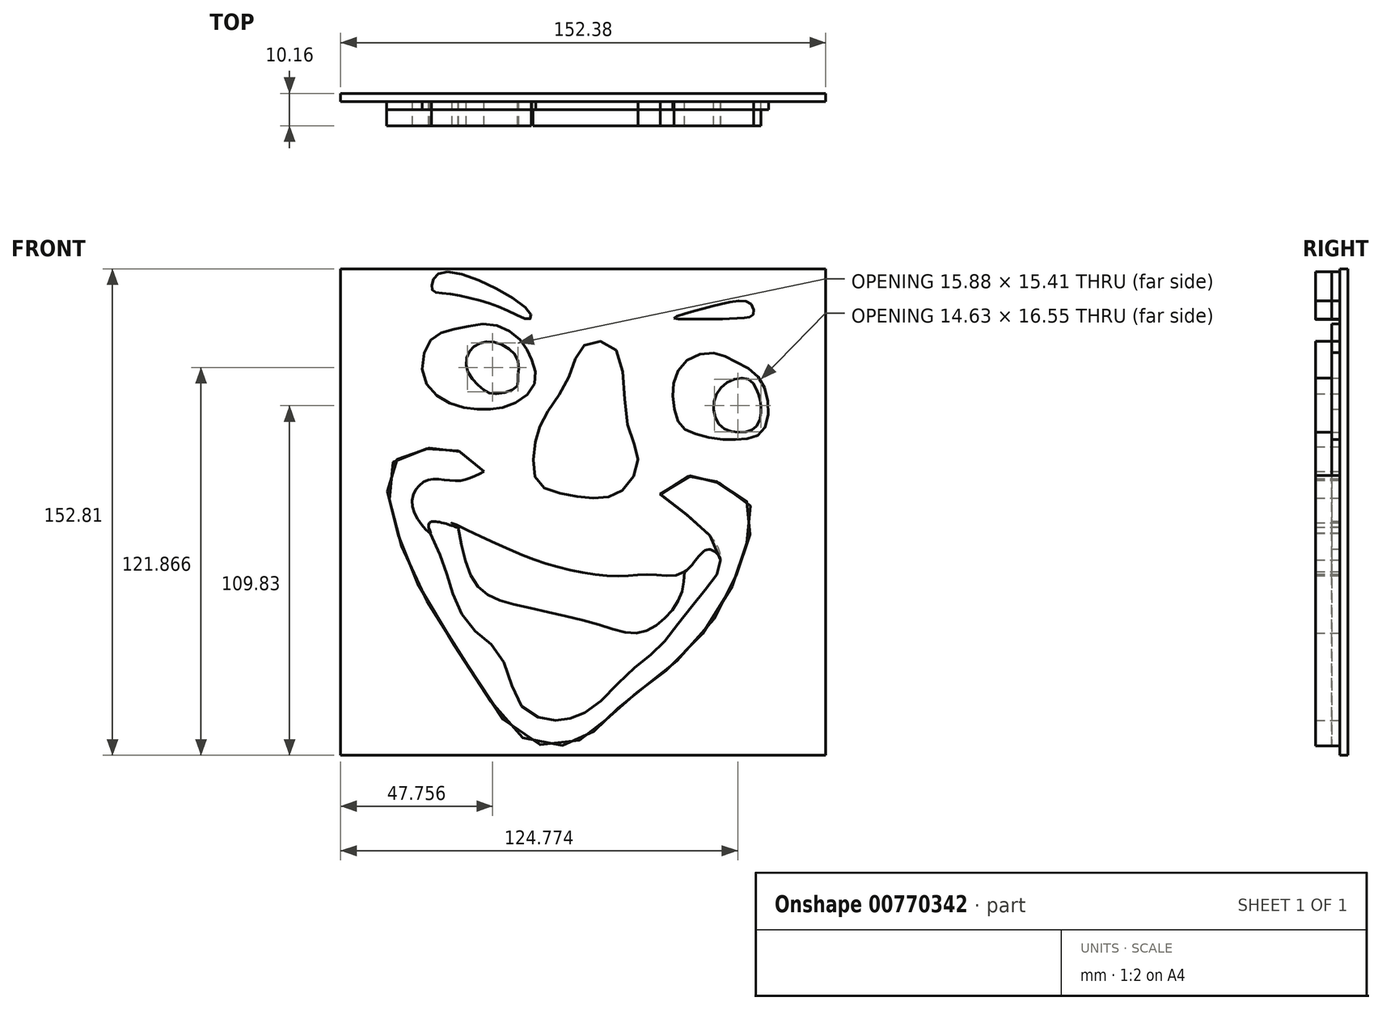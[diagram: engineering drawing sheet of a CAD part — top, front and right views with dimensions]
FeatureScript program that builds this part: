
annotation { "Feature Type Name" : "Feature", "Feature Type Description" : "" }
export const myFeature = defineFeature(function(context is Context, id is Id, definition is map)
    precondition{}
    {
        {
            var Q0;
            Q0=qCreatedBy(makeId("Front.planeOp"),FACE);
            var sketch = newSketch(context, id + "F0", { "sketchPlane" : qUnion([Q0])});
            skFitSpline(sketch, "E0", {"points": [v(-16.48, 48.25) * mm, v(-15.6, 40.6) * mm, v(-23.03, 34.06) * mm, v(-31.76, 32.75) * mm, v(-41.8, 34.5) * mm, v(-50.32, 42.57) * mm, v(-48.14, 54.58) * mm, v(-39.84, 58.07) * mm, v(-28.7, 59.38) * mm, v(-20.2, 54.58) * mm, v(-16.48, 48.25) * mm]});
            skFitSpline(sketch, "E1", {"points": [v(-25.87, 53.05) * mm, v(-32.2, 53.7) * mm, v(-36.13, 50.65) * mm, v(-36.78, 45.19) * mm, v(-32.42, 39.51) * mm, v(-27.83, 37.55) * mm, v(-21.29, 39.73) * mm, v(-20.85, 42.57) * mm, v(-20.85, 48.25) * mm, v(-25.87, 53.05) * mm]});
            skFitSpline(sketch, "E2", {"points": [v(40.71, 50.43) * mm, v(32.42, 48.25) * mm, v(28.27, 41.7) * mm, v(28.05, 34.27) * mm, v(30.24, 27.72) * mm, v(34.6, 25.1) * mm, v(42.9, 23.36) * mm, v(49.67, 23.36) * mm, v(54.9, 24.67) * mm, v(57.74, 29.9) * mm, v(57.09, 38.2) * mm, v(53.38, 44.32) * mm, v(46.4, 48.25) * mm, v(40.71, 50.43) * mm]});
            skFitSpline(sketch, "E3", {"points": [v(0, 52.83) * mm, v(-4.91, 42.57) * mm, v(-12.55, 30.13) * mm, v(-15.6, 20.74) * mm, v(-14.74, 10.04) * mm, v(-6.66, 6.11) * mm, v(3.6, 4.8) * mm, v(11.68, 6.99) * mm, v(16.92, 16.8) * mm, v(13.43, 28.82) * mm, v(9.71, 51.74) * mm, v(0, 52.83) * mm]});
            skFitSpline(sketch, "E4", {"points": [v(-42.9, 75.92) * mm, v(-17.14, 63.3) * mm, v(-17.14, 61.13) * mm, v(-24.12, 63.75) * mm, v(-33.95, 67.24) * mm, v(-43.99, 69.2) * mm, v(-47.48, 69.86) * mm, v(-47.7, 72.7) * mm, v(-42.9, 75.92) * mm]});
            skFitSpline(sketch, "E5", {"points": [v(28.27, 61.34) * mm, v(34.17, 63.53) * mm, v(44.64, 66.15) * mm, v(52.07, 66.15) * mm, v(53.16, 62.65) * mm, v(50.97, 61.56) * mm, v(44.43, 61.13) * mm, v(37.66, 61.13) * mm, v(28.27, 61.34) * mm]});
            skFitSpline(sketch, "E6", {"points": [v(-41.59, -3.06) * mm, v(-27.83, -9.39) * mm, v(-8.19, -16.81) * mm, v(9.71, -19.65) * mm, v(21.07, -19.21) * mm, v(31.55, -18.34) * mm, v(38.75, -11.35) * mm, v(42.9, -14.63) * mm, v(40.06, -21.4) * mm, v(31.98, -31.44) * mm, v(23.47, -42.13) * mm, v(14.52, -49.56) * mm, v(2.95, -60.9) * mm, v(-4.48, -64.4) * mm, v(-11.02, -64.84) * mm, v(-20.2, -59.82) * mm, v(-26.3, -44.54) * mm, v(-35.7, -35.59) * mm, v(-41.8, -23.36) * mm, v(-45.95, -11.35) * mm, v(-48.14, -2.62) * mm, v(-39.62, -4.37) * mm, v(-41.59, -3.06) * mm]});
            skFitSpline(sketch, "E7", {"points": [v(-39.62, -4.37) * mm, v(-33.51, -22.92) * mm, v(-19.98, -29.03) * mm, v(3.82, -34.7) * mm, v(16.7, -37.55) * mm, v(24.78, -33.4) * mm, v(30.23, -25.98) * mm, v(31.55, -18.34) * mm], "startDerivative": vector(22.86, -125.93) * mm, "endDerivative": vector(4.68, 71.43) * mm});
            skFitSpline(sketch, "E8", {"points": [v(-31.33, 13.1) * mm, v(-37.44, 18.56) * mm, v(-45.08, 20.96) * mm, v(-54.03, 19) * mm, v(-61.46, 14.2) * mm, v(-60.15, 0) * mm, v(-54.25, -18.34) * mm, v(-33.08, -53.26) * mm, v(-18.89, -70.73) * mm, v(-5.79, -72.7) * mm, v(3.16, -68.33) * mm, v(9.5, -62.22) * mm, v(20.2, -53.48) * mm, v(27.83, -47.59) * mm, v(43.99, -28.38) * mm, v(49.88, -12.66) * mm, v(53.16, 0) * mm, v(46.6, 7.2) * mm, v(37.44, 11.57) * mm, v(31.55, 11.35) * mm, v(23.9, 5.68) * mm, v(31.55, 0) * mm, v(37, -4.37) * mm, v(41.8, -10.26) * mm, v(42.9, -14.63) * mm], "startDerivative": vector(-165.3, 173.32) * mm, "endDerivative": vector(18.1, -166.15) * mm});
            skFitSpline(sketch, "E9", {"points": [v(-31.33, 13.32) * mm, v(-39.62, 10.26) * mm, v(-49.67, 10.26) * mm, v(-53.82, 1.75) * mm, v(-48.34, -6.17) * mm, v(-48.86, -4.37) * mm], "startDerivative": vector(-36.1, -20.12) * mm, "endDerivative": vector(-11.73, 26.34) * mm});
            skFitSpline(sketch, "E10", {"points": [v(51.63, 42.13) * mm, v(44.64, 41.04) * mm, v(40.71, 34.5) * mm, v(43.12, 27.29) * mm, v(49.67, 25.54) * mm, v(54.25, 27.5) * mm, v(55.56, 33.84) * mm, v(54.47, 38.2) * mm, v(51.63, 42.13) * mm]});
            skSolve(sketch);
        }
        {
            var Q0;
            Q0=makeQuery(id+"F0.imprint","IMPRINT",FACE,{"disambiguationData":[TD([[makeQuery(id+"F0.imprint","IMPRINT",EDGE,{"derivedFrom":sQuery(id+"F0.wireOp",EDGE,"E3")}),1.0]])]});
            var Q1;
            Q1=makeQuery(id+"F0.imprint","IMPRINT",FACE,{"disambiguationData":[TD([[makeQuery(id+"F0.imprint","IMPRINT",EDGE,{"derivedFrom":sQuery(id+"F0.wireOp",EDGE,"E4")}),-1.0]])]});
            var Q2;
            Q2=makeQuery(id+"F0.imprint","IMPRINT",FACE,{"disambiguationData":[TD([[makeQuery(id+"F0.imprint","IMPRINT",EDGE,{"derivedFrom":sQuery(id+"F0.wireOp",EDGE,"E5")}),-1.0]])]});
            var Q3;
            {var subQ0=sQuery(id+"F0.wireOp",EDGE,"E8");var subQ1=sQuery(id+"F0.wireOp",EDGE,"E6");var subQ2=makeQuery(id+"F0.imprint","INTERSECT",VERTEX,{"derivedFrom":[subQ1,subQ0]});Q3=makeQuery(id+"F0.imprint","IMPRINT",FACE,{"disambiguationData":[TD([[makeQuery(id+"F0.imprint","IMPRINT",EDGE,{"disambiguationData":[TD([[subQ2,-1.0]])],"derivedFrom":subQ1}),1.0]])]});}
            var Q4;
            {var subQ0=sQuery(id+"F0.wireOp",EDGE,"E9");var subQ1=sQuery(id+"F0.wireOp",EDGE,"E6");var subQ2=makeQuery(id+"F0.imprint","INTERSECT",VERTEX,{"disambiguationData":[OD(0.0)],"derivedFrom":[subQ1,subQ0]});Q4=makeQuery(id+"F0.imprint","IMPRINT",FACE,{"disambiguationData":[TD([[makeQuery(id+"F0.imprint","IMPRINT",EDGE,{"disambiguationData":[TD([[subQ2,1.0]])],"derivedFrom":subQ1}),-1.0]])]});}
            var Q5;
            Q5=makeQuery(id+"F0.imprint","IMPRINT",FACE,{"disambiguationData":[TD([[makeQuery(id+"F0.imprint","IMPRINT",EDGE,{"derivedFrom":sQuery(id+"F0.wireOp",EDGE,"E10")}),1.0]])]});
            var Q6;
            Q6=makeQuery(id+"F0.imprint","IMPRINT",FACE,{"disambiguationData":[TD([[makeQuery(id+"F0.imprint","IMPRINT",EDGE,{"derivedFrom":sQuery(id+"F0.wireOp",EDGE,"E1")}),1.0]])]});
            var Q7;
            {var subQ0=sQuery(id+"F0.wireOp",EDGE,"E7");Q7=makeQuery(id+"F0.imprint","IMPRINT",FACE,{"disambiguationData":[TD([[makeQuery(id+"F0.imprint","IMPRINT",EDGE,{"derivedFrom":subQ0}),1.0]])]});}
            extrude(context, id + "F1", {"entities" : qUnion([Q0, Q1, Q2, Q3, Q4, Q5, Q6, Q7]), "depth" : 7.62 * mm, "offsetDistance" : 25.4 * mm});
        }
        {
            var Q0;
            Q0 = qSketchRegion(id + "F0", true);
            extrude(context, id + "F2", {"entities" : qUnion([Q0]), "depth" : 2.54 * mm, "offsetDistance" : 25.4 * mm});
        }
        {
            var Q0;
            Q0=qCreatedBy(makeId("Front.planeOp"),FACE);
            var sketch = newSketch(context, id + "F3", { "sketchPlane" : qUnion([Q0])});
            skLineSegment(sketch, "E11.bottom", {"start": v(-76.52, 76.84) * mm, "end": v(75.86, 76.84) * mm});
            skLineSegment(sketch, "E11.top", {"start": v(-76.52, -75.97) * mm, "end": v(75.86, -75.97) * mm});
            skLineSegment(sketch, "E11.left", {"start": v(-76.52, 76.84) * mm, "end": v(-76.52, -75.97) * mm});
            skLineSegment(sketch, "E11.right", {"start": v(75.86, 76.84) * mm, "end": v(75.86, -75.97) * mm});
            skSolve(sketch);
        }
        {
            var Q0;
            Q0 = qSketchRegion(id + "F3", true);
            extrude(context, id + "F4", {"entities" : qUnion([Q0]), "oppositeDirection" : true, "depth" : 2.54 * mm, "offsetDistance" : 25.4 * mm});
        }
    });
